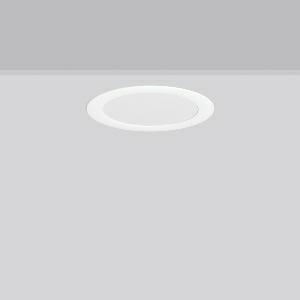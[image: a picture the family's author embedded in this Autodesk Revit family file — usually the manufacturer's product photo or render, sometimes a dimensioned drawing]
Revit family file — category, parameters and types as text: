
# Revit family: toledo_flat_round_e_672224_002_04_aff2
name_source: partatom
category: Lighting Fixtures
units: mm (PartAtom-declared; Revit-internal decimal feet)

## family parameters
Cut with Voids When Loaded = No
Host = Face
Light Source = No
Part Type = Normal
Room Calculation Point = No
Round Connector Dimension = Use Diameter
Shared = No

## types (1)
- TOLEDO FLAT round E (1 x LED Modul 830, 1650 lm, 3000)
    Apparent Load = 17 VA
    CIE Flux Codes = 48 79 96 100 100
    Color Rendering = 80
    Color Temperature = 3000
    Default Elevation = 1800 mm
    Description = Series: TOLEDO FLAT round
Ultra thin recessed downlight. For escape route illumination. Housing: die-cast aluminium, powder-coated. Lightguide and diffuser made of non-yellowing plastic (PMMA). Diffuser opal matt plastic. Ceiling installation with spring system. Including separate LED converter with connecting cable 250 mm. Self-contained system with automatic self-test and feedback to the RZB monitoring system MULTIDIGIT. External driver with simple plug-in locking system. 
Colour: white
Diameter: 255 mm
Height: 3 mm
Cut-out diameter: 234 mm
Recess height: 100 mm
Luminaire: recess height: 60-80 mm
Weight: 1.77 kg
Operating mode: maintained power mode
Duration time: 3 h
Lamp: LED
Socket: without socket
Colour temperature: 3000K
Colour rendering index (CRI): 80
System power: 17 W
Rated luminous flux: 1650 lm
Luminous flux, emergency: 450 lm
System power, emergency: -
Control gear: Regulated power supply
Protection class: I
Type of protection: IP 54
    Height = 0 mm  [stored 0 ft]
    Lamp = 1 x LED Modul 830
    Lamp Light Flux = 1650 lm
    Lamp count = 1
    Length = 255 mm
    Lifetime = 50000 h
    Luminous efficacy = 97 lm/W
    Manufacturer = RZB
    ModVariant = No
    Model = 672224.002.04
    Mounting Place = Ceiling
    Mounting Type = Recessed
    Number of Poles = 1
    OnlyDefault = Yes
    Power Factor = 1
    Product Name = TOLEDO FLAT round E
    Product group = Recessed downlights
    ProductGroupID = 402
    Protection Class = Protection class I
    Protection Degree = IP 40
    RLX_Detail_Level = 1
    RLX_Emergency_Light_Flux = 450 lm
    RLX_Emergency_Type = 3
    RLX_Emergency_Type_DB = Yes
    RlxData = <blob elided: 30349 chars, md5=a6e3b9fd>
    Socket = socket
    Standby Power = 0 W
    System Light Flux = 1650 lm
    System Power = 17 W
    Type Comments = Product without accessories
    Type Image = 901453.002.jpg
    URL = http://relux.com
    VarID = ---
    Voltage = 0 V
    Weight = 0.00 kg
    Width = 0 mm  [stored 0 ft]

note: [stored X ft] marks values corroborated as IEEE doubles in the binary element streams (Revit-internal decimal feet)

## geometry (parser evidence)
native form markers: Blend x4, Sweep x12
no freeform markers — native parametric forms only
